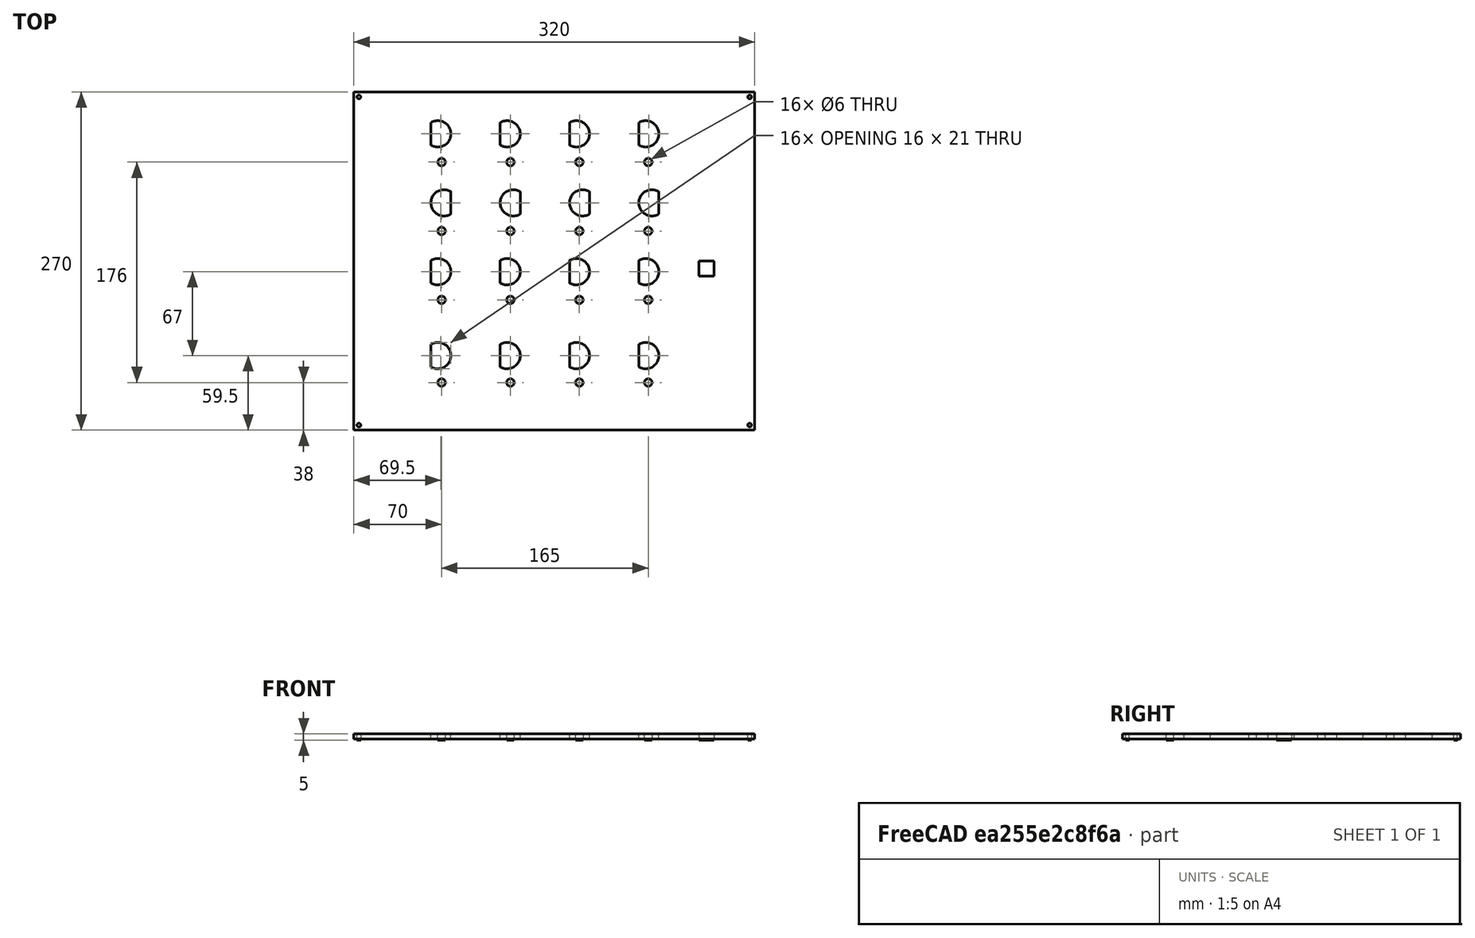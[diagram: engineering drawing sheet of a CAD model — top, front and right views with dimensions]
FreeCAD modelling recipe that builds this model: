
FCSTD DOCUMENT  (FreeCAD 0.14R3700 (Git))
Label: interFace-4mm (2)
License: CC-BY 3.0
LicenseURL: http://creativecommons.org/licenses/by/3.0/
objects: Sketcher::SketchObject×9, PartDesign::Pocket×5, PartDesign::Pad×4, Part::Offset×4, Part::FeaturePython×4, Part::Cut×4, Part::Box×1, Mesh::Feature×1, PartDesign::LinearPattern×1
note: 41 computed .brp shape members not serialized (recipe doc carries the construction recipe); baked Part::Feature solids carry a one-line shape summary decoded from their .brp

FEATURE [Part::Box] Box  label="Cubo"
  Height = 4
  Length = 320
  Width = 270
FEATURE [Sketcher::SketchObject] Sketch004
  ExternalGeometry = -> [Box]
  Placement = pos=(0,0,4) rot=(0,0,1;0rad)
  Support = -> Box [Face6]
  sketch-geometry (4):
    g0: Circle CenterX=70 CenterY=214 CenterZ=0 NormalX=0 NormalY=0 NormalZ=1 Radius=3
    g1: Circle CenterX=125 CenterY=214 CenterZ=0 NormalX=0 NormalY=0 NormalZ=1 Radius=3
    g2: Circle CenterX=180 CenterY=214 CenterZ=0 NormalX=0 NormalY=0 NormalZ=1 Radius=3
    g3: Circle CenterX=235 CenterY=214 CenterZ=0 NormalX=0 NormalY=0 NormalZ=1 Radius=3
  constraints (12):
    c: Equal(g0,g1)
    c: Equal(g1,g3)
    c: Radius(g3) = 3
    c: DistanceY(g0,g-3) = 56
    c: DistanceY(g1,g-3) = 56
    c: DistanceX(g0,g-3) = -70
    c: DistanceX(g0,g1) = 55
    c: DistanceX(g1,g2) = 55
    c: DistanceX(g2,g3) = 55
    c: DistanceY(g3,g-3) = 56
    c: DistanceY(g2,g-3) = 56
    c: Equal(g2,g3)
FEATURE [Sketcher::SketchObject] Sketch008
  Placement = pos=(57,251.5,-1) rot=(0,0,-1;1.5708rad)
  sketch-geometry (2):
    g0: ArcOfCircle CenterX=15 CenterY=10 CenterZ=0 NormalX=0 NormalY=0 NormalZ=1 Radius=10 StartAngle=5.75959 EndAngle=9.94838
    g1: LineSegment StartX=6.33975 StartY=5 StartZ=0 EndX=23.6603 EndY=5 EndZ=0
  constraints (7):
    c: Radius(g0) = 10
    c: Horizontal(g1)
    c: PointOnObject(g0,g1)
    c: PointOnObject(g0,g1)
    c: Coincident(g1,g0)
    c: Coincident(g1,g0)
    c: DistanceY(g0,g0) = 5
FEATURE [PartDesign::Pad] Pad
  Length = 7
  Length2 = 100
  Placement = pos=(57,251.5,-1) rot=(0,0,-1;1.5708rad)
  Sketch = -> Sketch008
  Type = 0
FEATURE [Mesh::Feature] fichaLab3y  label="fichaLab3y4"
  Placement = pos=(127.33,181.5,-0.5) rot=(0,0,1;0rad)
FEATURE [PartDesign::Pocket] Pocket
  Length = 5
  Sketch = -> Sketch004
  Type = 0
FEATURE [PartDesign::LinearPattern] LinearPattern
  Direction = -> Sketch004 [V_Axis]
  Length = 110
  Occurrences = 3
  Originals = -> [Pocket]
  Reversed = true
FEATURE [Sketcher::SketchObject] Sketch005
  Placement = pos=(0,0,4) rot=(0,0,1;0rad)
  Support = -> LinearPattern [Face3]
  sketch-geometry (4):
    g0: Circle CenterX=70 CenterY=38 CenterZ=0 NormalX=0 NormalY=0 NormalZ=1 Radius=3
    g1: Circle CenterX=125 CenterY=38 CenterZ=0 NormalX=0 NormalY=0 NormalZ=1 Radius=3
    g2: Circle CenterX=180 CenterY=38 CenterZ=0 NormalX=0 NormalY=0 NormalZ=1 Radius=3
    g3: Circle CenterX=235 CenterY=38 CenterZ=0 NormalX=0 NormalY=0 NormalZ=1 Radius=3
  constraints (12):
    c: Equal(g0,g1)
    c: Equal(g1,g2)
    c: Equal(g2,g3)
    c: Radius(g0) = 3
    c: DistanceX(g-1,g0) = 70
    c: DistanceY(g-1,g0) = 38
    c: DistanceX(g0,g1) = 55
    c: DistanceY(g-1,g1) = 38
    c: DistanceX(g2,g1) = -55
    c: DistanceY(g-1,g2) = 38
    c: DistanceY(g-1,g3) = 38
    c: DistanceX(g3,g2) = -55
FEATURE [PartDesign::Pocket] Pocket001
  Length = 5
  Sketch = -> Sketch005
  Type = 0
FEATURE [Sketcher::SketchObject] Sketch007
  ExternalGeometry = -> [Pocket001]
  Placement = pos=(0,0,4) rot=(0,0,1;0rad)
  Support = -> Pocket001 [Face3]
  sketch-geometry (16):
    g0: Circle CenterX=67 CenterY=236.5 CenterZ=0 NormalX=0 NormalY=0 NormalZ=1 Radius=2
    g1: Circle CenterX=122.333 CenterY=236.5 CenterZ=0 NormalX=0 NormalY=0 NormalZ=1 Radius=2
    g2: Circle CenterX=177.667 CenterY=236.5 CenterZ=0 NormalX=0 NormalY=0 NormalZ=1 Radius=2
    g3: Circle CenterX=233 CenterY=236.5 CenterZ=0 NormalX=0 NormalY=0 NormalZ=1 Radius=2
    g4: Circle CenterX=72 CenterY=181.5 CenterZ=0 NormalX=0 NormalY=0 NormalZ=1 Radius=2
    g5: Circle CenterX=127.333 CenterY=181.5 CenterZ=0 NormalX=0 NormalY=0 NormalZ=1 Radius=2
    g6: Circle CenterX=182.667 CenterY=181.5 CenterZ=0 NormalX=0 NormalY=0 NormalZ=1 Radius=2
    g7: Circle CenterX=238 CenterY=181.5 CenterZ=0 NormalX=0 NormalY=0 NormalZ=1 Radius=2
    g8: Circle CenterX=67 CenterY=126.5 CenterZ=0 NormalX=0 NormalY=0 NormalZ=1 Radius=2
    g9: Circle CenterX=122.333 CenterY=126.5 CenterZ=0 NormalX=0 NormalY=0 NormalZ=1 Radius=2
    g10: Circle CenterX=177.667 CenterY=126.5 CenterZ=0 NormalX=0 NormalY=0 NormalZ=1 Radius=2
    g11: Circle CenterX=233 CenterY=126.5 CenterZ=0 NormalX=0 NormalY=0 NormalZ=1 Radius=2
    g12: Circle CenterX=67 CenterY=59.5 CenterZ=0 NormalX=0 NormalY=0 NormalZ=1 Radius=2
    g13: Circle CenterX=122.333 CenterY=59.5 CenterZ=0 NormalX=0 NormalY=0 NormalZ=1 Radius=2
    g14: Circle CenterX=177.667 CenterY=59.5 CenterZ=0 NormalX=0 NormalY=0 NormalZ=1 Radius=2
    g15: Circle CenterX=233 CenterY=59.5 CenterZ=0 NormalX=0 NormalY=0 NormalZ=1 Radius=2
  constraints (48):
    c: Equal(g0,g1)
    c: Equal(g1,g3)
    c: Equal(g3,g2)
    c: Radius(g0) = 2
    c: Equal(g7,g6)
    c: Equal(g6,g5)
    c: Equal(g5,g4)
    c: Radius(g7) = 2
    c: Equal(g11,g10)
    c: Equal(g10,g9)
    c: Equal(g9,g8)
    c: Radius(g11) = 2
    c: Equal(g15,g14)
    c: Equal(g14,g13)
    c: Equal(g13,g12)
    c: Radius(g15) = 2
    c: DistanceX(g0,g1) = 55.3333
    c: DistanceX(g1,g2) = 55.3334
    c: DistanceX(g2,g3) = 55.3333
    c: DistanceY(g0,g-3) = 33.5
    c: DistanceY(g1,g-3) = 33.5
    c: DistanceY(g3,g-3) = 33.5
    c: DistanceY(g2,g-3) = 33.5
    c: DistanceX(g4,g5) = 55.3333
    c: DistanceX(g5,g6) = 55.3334
    c: DistanceX(g6,g7) = 55.3333
    c: DistanceY(g4,g-3) = 88.5
    c: DistanceY(g5,g-3) = 88.5
    c: DistanceY(g7,g-3) = 88.5
    c: DistanceY(g6,g-3) = 88.5
    c: DistanceX(g8,g9) = 55.3333
    c: DistanceX(g9,g10) = 55.3334
    c: DistanceX(g10,g11) = 55.3333
    c: DistanceY(g8,g-3) = 143.5
    c: DistanceY(g9,g-3) = 143.5
    c: DistanceY(g11,g-3) = 143.5
    c: DistanceY(g10,g-3) = 143.5
    c: DistanceX(g12,g13) = 55.3333
    c: DistanceX(g13,g14) = 55.3333
    c: DistanceX(g14,g15) = 55.3334
    c: DistanceY(g12,g-3) = 210.5
    c: DistanceY(g13,g-3) = 210.5
    c: DistanceY(g14,g-3) = 210.5
    c: DistanceY(g15,g-3) = 210.5
    c: DistanceX(g15,g-3) = 87
    c: DistanceX(g0,g-3) = -67
    c: DistanceX(g4,g-3) = -72
    c: DistanceX(g11,g-3) = 87
FEATURE [PartDesign::Pocket] Pocket002
  Length = 5
  Sketch = -> Sketch007
  Type = 0
FEATURE [Part::Offset] Offset
  Fill = false
  Intersection = false
  Join = 0
  Mode = 0
  SelfIntersection = false
  Source = -> Pad
  Value = 0.5
FEATURE [Part::FeaturePython] Array  # Draft array (typed FeaturePython)
  Angle = 360
  ArrayType = 0
  Axis = (0,0,1)
  Base = -> Offset
  Center = (0,0,0)
  IntervalX = (55.33,0,0)
  IntervalY = (0,1,0)
  IntervalZ = (0,0,1)
  NumberPolar = 1
  NumberX = 4
  NumberY = 1
  NumberZ = 1
FEATURE [Part::Cut] Cut
  Base = -> Pocket002
  Tool = -> Array
FEATURE [Sketcher::SketchObject] Sketch
  Placement = pos=(57,141.5,-1) rot=(0,0,-1;1.5708rad)
  sketch-geometry (2):
    g0: ArcOfCircle CenterX=15 CenterY=10 CenterZ=0 NormalX=0 NormalY=0 NormalZ=1 Radius=10 StartAngle=5.75959 EndAngle=9.94838
    g1: LineSegment StartX=6.33975 StartY=5 StartZ=0 EndX=23.6603 EndY=5 EndZ=0
  constraints (7):
    c: Radius(g0) = 10
    c: Horizontal(g1)
    c: PointOnObject(g0,g1)
    c: PointOnObject(g0,g1)
    c: Coincident(g1,g0)
    c: Coincident(g1,g0)
    c: DistanceY(g0,g0) = 5
FEATURE [PartDesign::Pad] Pad001
  Length = 7
  Length2 = 100
  Placement = pos=(57,141.5,-1) rot=(0,0,-1;1.5708rad)
  Sketch = -> Sketch
  Type = 0
FEATURE [Part::Offset] Offset001
  Fill = false
  Intersection = false
  Join = 0
  Mode = 0
  SelfIntersection = false
  Source = -> Pad001
  Value = 0.5
FEATURE [Part::FeaturePython] Array001  # Draft array (typed FeaturePython)
  Angle = 360
  ArrayType = 0
  Axis = (0,0,1)
  Base = -> Offset001
  Center = (0,0,0)
  IntervalX = (55.33,0,0)
  IntervalY = (0,1,0)
  IntervalZ = (0,0,1)
  NumberPolar = 1
  NumberX = 4
  NumberY = 1
  NumberZ = 1
FEATURE [Part::Cut] Cut001
  Base = -> Cut
  Tool = -> Array001
FEATURE [Sketcher::SketchObject] Sketch009
  Placement = pos=(57,74.5,-1) rot=(0,0,-1;1.5708rad)
  sketch-geometry (2):
    g0: ArcOfCircle CenterX=15 CenterY=10 CenterZ=0 NormalX=0 NormalY=0 NormalZ=1 Radius=10 StartAngle=5.75959 EndAngle=9.94838
    g1: LineSegment StartX=6.33975 StartY=5 StartZ=0 EndX=23.6603 EndY=5 EndZ=0
  constraints (7):
    c: Radius(g0) = 10
    c: Horizontal(g1)
    c: PointOnObject(g0,g1)
    c: PointOnObject(g0,g1)
    c: Coincident(g1,g0)
    c: Coincident(g1,g0)
    c: DistanceY(g0,g0) = 5
FEATURE [PartDesign::Pad] Pad002
  Length = 7
  Length2 = 100
  Placement = pos=(57,74.5,-1) rot=(0,0,-1;1.5708rad)
  Sketch = -> Sketch009
  Type = 0
FEATURE [Part::Offset] Offset002
  Fill = false
  Intersection = false
  Join = 0
  Mode = 0
  SelfIntersection = false
  Source = -> Pad002
  Value = 0.5
FEATURE [Part::FeaturePython] Array002  # Draft array (typed FeaturePython)
  Angle = 360
  ArrayType = 0
  Axis = (0,0,1)
  Base = -> Offset002
  Center = (0,0,0)
  IntervalX = (55.33,0,0)
  IntervalY = (0,1,0)
  IntervalZ = (0,0,1)
  NumberPolar = 1
  NumberX = 4
  NumberY = 1
  NumberZ = 1
FEATURE [Part::Cut] Cut002
  Base = -> Cut001
  Tool = -> Array002
FEATURE [Sketcher::SketchObject] Sketch010
  Placement = pos=(82,166.5,-1) rot=(0,0,1;1.5708rad)
  sketch-geometry (2):
    g0: ArcOfCircle CenterX=15 CenterY=10 CenterZ=0 NormalX=0 NormalY=0 NormalZ=1 Radius=10 StartAngle=5.75959 EndAngle=9.94838
    g1: LineSegment StartX=6.33975 StartY=5 StartZ=0 EndX=23.6603 EndY=5 EndZ=0
  constraints (7):
    c: Radius(g0) = 10
    c: Horizontal(g1)
    c: PointOnObject(g0,g1)
    c: PointOnObject(g0,g1)
    c: Coincident(g1,g0)
    c: Coincident(g1,g0)
    c: DistanceY(g0,g0) = 5
FEATURE [PartDesign::Pad] Pad003
  Length = 7
  Length2 = 100
  Placement = pos=(82,166.5,-1) rot=(0,0,1;1.5708rad)
  Sketch = -> Sketch010
  Type = 0
FEATURE [Part::Offset] Offset003
  Fill = false
  Intersection = false
  Join = 0
  Mode = 0
  SelfIntersection = false
  Source = -> Pad003
  Value = 0.5
FEATURE [Part::FeaturePython] Array003  # Draft array (typed FeaturePython)
  Angle = 360
  ArrayType = 0
  Axis = (0,0,1)
  Base = -> Offset003
  Center = (0,0,0)
  IntervalX = (55.33,0,0)
  IntervalY = (0,1,0)
  IntervalZ = (0,0,1)
  NumberPolar = 1
  NumberX = 4
  NumberY = 1
  NumberZ = 1
FEATURE [Part::Cut] Cut003
  Base = -> Cut002
  Tool = -> Array003
FEATURE [Sketcher::SketchObject] Sketch011
  ExternalGeometry = -> [Cut003]
  Placement = pos=(0,0,4) rot=(0,0,1;0rad)
  Support = -> Cut003 [Face3]
  sketch-geometry (4):
    g0: LineSegment StartX=275.5 StartY=135 StartZ=0 EndX=287.5 EndY=135 EndZ=0
    g1: LineSegment StartX=287.5 StartY=135 StartZ=0 EndX=287.5 EndY=123 EndZ=0
    g2: LineSegment StartX=287.5 StartY=123 StartZ=0 EndX=275.5 EndY=123 EndZ=0
    g3: LineSegment StartX=275.5 StartY=123 StartZ=0 EndX=275.5 EndY=135 EndZ=0
  constraints (14):
    c: Coincident(g0,g1)
    c: Coincident(g1,g2)
    c: Coincident(g2,g3)
    c: Coincident(g3,g0)
    c: Horizontal(g0)
    c: Horizontal(g2)
    c: Vertical(g1)
    c: Vertical(g3)
    c: Equal(g0,g2)
    c: Equal(g2,g1)
    c: Equal(g1,g3)
    c: DistanceX(g0) = 12
    c: DistanceX(g1,g-3) = 32.5
    c: DistanceY(g1,g-3) = -123
FEATURE [PartDesign::Pocket] Pocket003  label="interFace-4mm(2)"
  Length = 5
  Sketch = -> Sketch011
  Type = 0
FEATURE [Sketcher::SketchObject] Sketch012
  ExternalGeometry = -> [Pocket003]
  Placement = pos=(0,0,4) rot=(0,0,1;0rad)
  Support = -> Pocket003 [Face3]
  sketch-geometry (4):
    g0: Circle CenterX=4 CenterY=4 CenterZ=0 NormalX=0 NormalY=0 NormalZ=1 Radius=1.5
    g1: Circle CenterX=4 CenterY=266 CenterZ=0 NormalX=0 NormalY=0 NormalZ=1 Radius=1.5
    g2: Circle CenterX=316 CenterY=266 CenterZ=0 NormalX=0 NormalY=0 NormalZ=1 Radius=1.5
    g3: Circle CenterX=316 CenterY=4 CenterZ=0 NormalX=0 NormalY=0 NormalZ=1 Radius=1.5
  constraints (12):
    c: Radius(g0) = 1.5
    c: DistanceY(g-1,g0) = 4
    c: DistanceX(g-1,g0) = 4
    c: Radius(g1) = 1.5
    c: DistanceY(g1,g-3) = 4
    c: DistanceX(g1,g-3) = -4
    c: Radius(g2) = 1.5
    c: DistanceY(g2,g-3) = 4
    c: DistanceX(g2,g-3) = 4
    c: Radius(g3) = 1.5
    c: DistanceY(g3,g-4) = -4
    c: DistanceX(g3,g-4) = 4
FEATURE [PartDesign::Pocket] Pocket004  label="interFace-4mm(2)001"
  Length = 5
  Sketch = -> Sketch012
  Type = 0
